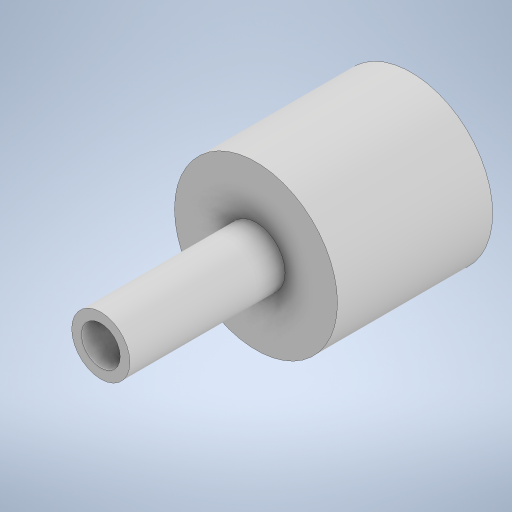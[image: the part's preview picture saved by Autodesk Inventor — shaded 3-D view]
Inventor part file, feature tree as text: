
AUTODESK INVENTOR PART (.ipt)
format: ipt  version: 2023 (Build 270158000, 158)  size: 367,616 bytes
history: native  units: mm
features: extrude x2, sketch x1
ambient origin geometry x8: Origin, YZ Plane, XZ Plane, XY Plane, X Axis, Y Axis, Z Axis, Center Point
bodies: Body1 (feature_tree)
feature tree (3):
  sketch  "Sketch1"  dims[d0=21.0mm d1=5.0mm d4=7.5mm d13=20.0mm d14=0.0mm d15=20.0mm d16=0.0mm]
  extrude  "Extrusion6"  Depth=20.0mm
  extrude  "Extrusion7"  Depth=20.0mm
